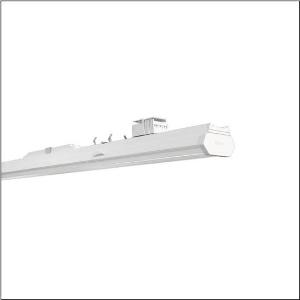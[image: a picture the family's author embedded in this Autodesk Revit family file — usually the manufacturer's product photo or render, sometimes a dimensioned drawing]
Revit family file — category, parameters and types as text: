
# Revit family: licross_11_protected_ho_51tp12cn4exm
name_source: partatom
category: Lighting Fixtures
units: mm (PartAtom-declared; Revit-internal decimal feet)

## family parameters
Cut with Voids When Loaded = No
Host = Face
Light Source = No
Part Type = Normal
Room Calculation Point = No
Round Connector Dimension = Use Diameter
Shared = No

## types (1)
- --- (1 x LED, 14240 lm, 77.6 W, 4000K)
    Apparent Load = 78 VA
    CIE Flux Codes = 70 91 97 98 100
    Color Rendering = 80
    Color Temperature = 4000K
    Default Elevation = 1800 mm
    Description = Licross 11 Protected HO, luminaire insert, of sheet steel, galvanised, coil coated, white, length: 1.500mm, width: 90mm, height: 101mm, LED rated luminous flux: 14.240lm, light colour: 840, SDCM (Standard Deviation of Colour Matching)MacAdam ≤ 2 SDCM (initial), control gear: ON/OFF Multilumen, CLOi, with plug, 3-pole, with phase selection, mains connection: 220..240V, AC, 50/60Hz, start of lifetime: 78W, end of service life: 87W, internal wiring halogen-free, primary light control with lens, of plastic, primary optical cover: cover, of PMMA, light emission: direct distribution, primary light characteristic: symmetric, protection rating (complete): IP64, insulation class (complete): insulation class I (protective earthing), certification: CE, ENEC, VDE, UKCA, protection symbol: D if used in an environment with conductive dust loads with corresponding accessories, impact resistance: IK06, permissible ambient temperature for indoor applications: -35..+35°C, corresponds to IFS (International Featured Standards) requirements for safety and quality in the food industry, reducing of maximum allowable ambient temperature of 5°C with ceiling mounting, LABS conformity tested according to VDMA 24364:2018-05, The light source and the operating device comply with the requirements of the Ecodesign Regulation (EU) 2019/2020 and are replaceable in accordance with this regulation, packaging unit: 1 piece
    Height = 92 mm
    Lamp = 1 x LED
    Lamp Light Flux = 14240 lm
    Lamp Power = 77.6 W
    Lamp count = 1
    Length = 1500 mm
    Luminous efficacy = 184 lm/W
    Manufacturer = Siteco
    ModVariant = No
    Model = 51TP12CN4EXM
    Mounting Place = Ceiling
    Mounting Type = Pendant
    Number of Poles = 1
    OnlyDefault = Yes
    Power Factor = 1
    Product Name = Licross 11 Protected HO
    Product group = luminaire insert | ceiling pendant
    ProductGroupID = 901
    Protection Class = Protection class I
    Protection Degree = IP 64
    RLX_Detail_Level = 1
    RLX_Emergency_Light_Flux = 0 lm
    RLX_Emergency_Type = 0
    RLX_Emergency_Type_DB = No
    RlxData = <blob elided: 22489 chars, md5=77bd6435>
    Socket = socket
    Standby Power = 0 W
    System Light Flux = 14240 lm
    System Power = 78 W
    Type Comments = factory setting: luminous flux: 100 % | (A | C | E) | 181 mA
    Type Image = l_1256148.jpg
    URL = http://relux.com
    VarID = @adj_000903
    Voltage = 0 V
    Weight = 0.00 kg
    Width = 88 mm

## geometry (parser evidence)
native form markers: Blend x4, Sweep x9
no freeform markers — native parametric forms only
